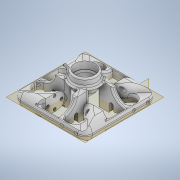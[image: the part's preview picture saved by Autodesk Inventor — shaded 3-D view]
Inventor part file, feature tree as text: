
AUTODESK INVENTOR PART (.ipt)
format: ipt  version: 2020 (Build 240168000, 168)  size: 1,643,520 bytes
history: native  units: mm
features: fillet x26, sketch x14, extrude x12, revolve x8, hole x4, plane x2, chamfer x1
ambient origin geometry x8: Origin, YZ Plane, XZ Plane, XY Plane, X Axis, Y Axis, Z Axis, Center Point
bodies: Solid1 (feature_tree)
feature tree (67):
  sketch  "Sketch1"  dims[d0=22.0mm d3=15.556349mm]
  revolve  "Revolution1"  [1 undecoded]
  revolve  "Revolution2"  [1 undecoded]
  revolve  "Revolution3"  [1 undecoded]
  revolve  "Revolution4"  [1 undecoded]
  plane  "Work Plane1"
  sketch  "Sketch2"  dims[d4=15.556349mm d5=40.0mm]
  extrude  "Extrusion2"  Depth=13.0mm
  chamfer  "Chamfer1"  Distance=40.0mm
  fillet  "Fillet2"  [1 undecoded]
  extrude  "Extrusion3"  TaperAngle=135.0deg  [1 undecoded]
  extrude  "Extrusion5"  Depth=5.0mm TaperAngle=360.0deg
  fillet  "Fillet3"  [1 undecoded]
  fillet  "Fillet4"  [1 undecoded]
  fillet  "Fillet5"  [1 undecoded]
  fillet  "Fillet6"  [1 undecoded]
  hole  "Hole2"  [1 undecoded]
  hole  "Hole3"  [1 undecoded]
  hole  "Hole4"  [1 undecoded]
  fillet  "Fillet7"  Radius=100.0mm
  hole  "Hole5"  [1 undecoded]
  plane  "Work Plane2"
  sketch  "Sketch13"  dims[d13=31.5mm]
  extrude  "Extrusion9"  Depth=5.0mm
  extrude  "Extrusion10"  Depth=10.0mm TaperAngle=0.0deg
  fillet  "Fillet8"  Radius=10.0mm
  fillet  "Fillet9"  Radius=2.0mm
  fillet  "Fillet10"  Radius=22.0mm
  revolve  "Revolution9"  [1 undecoded]
  revolve  "Revolution10"  [1 undecoded]
  revolve  "Revolution11"  [1 undecoded]
  revolve  "Revolution12"  [1 undecoded]
  extrude  "Extrusion11"  Depth=10.0mm
  fillet  "Fillet11"  Radius=16.0mm
  fillet  "Fillet12"  Radius=19.0mm
  fillet  "Fillet13"  Radius=19.0mm
  extrude  "Extrusion12"  Depth=5.0mm
  fillet  "Fillet14"  Radius=16.0mm
  fillet  "Fillet15"  Radius=19.0mm
  extrude  "Extrusion13"  Depth=5.0mm
  fillet  "Fillet17"  Radius=3.0mm
  fillet  "Fillet18"  Radius=19.0mm
  fillet  "Fillet19"  Radius=16.0mm
  fillet  "Fillet20"  Radius=40.0mm
  extrude  "Extrusion14"  Depth=5.0mm
  fillet  "Fillet21"  Radius=3.221825mm
  extrude  "Extrusion15"  Depth=5.0mm
  fillet  "Fillet22"  Radius=28.0mm
  extrude  "Extrusion16"  Depth=5.0mm
  fillet  "Fillet23"  Radius=6.0mm
  fillet  "Fillet24"  Radius=6.0mm
  extrude  "Extrusion17"  Depth=5.0mm
  fillet  "Fillet25"  Radius=21.0mm
  fillet  "Fillet26"  Radius=10.0mm
  fillet  "Fillet30"  Radius=20.0mm
  fillet  "Fillet31"  Radius=6.0mm
  sketch  "Sketch3"  dims[d6=3.221825mm d7=3.222mm]
  sketch  "Sketch4"  dims[d8=18.5mm d9=28.0mm]
  sketch  "Sketch6"  dims[d10=4.0mm d11=13.0mm]
  sketch  "Sketch7"  dims[d12=5.0mm]
  sketch  "Sketch14"  dims[d14=2.778175mm]
  sketch  "Sketch16"  dims[d15=2.778mm]
  sketch  "Sketch17"  dims[d16=14.0mm]
  sketch  "Sketch18"  dims[d17=19.0mm]
  sketch  "Sketch19"  dims[d18=3.0mm]
  sketch  "Sketch20"  dims[d19=25.0mm]
  sketch  "Sketch21"  dims[d20=135.0deg d21=40.0mm d22=135.0deg d23=135.0deg d24=40.0mm d26=360.0deg d28=90.0deg d29=90.0deg d30=90.0deg d31=90.0deg d38=19.0mm d39=16.0mm d50=100.0mm d51=100.0mm d52=96.0mm d53=96.0mm d54=10.0mm d55=0.0mm d56=10.0mm d57=2.0mm d58=45.0deg d59=2.0mm d60=22.0mm d61=0.0mm d64=22.0mm d65=0.0mm d66=10.0mm d67=10.0mm d68=10.0mm d69=10.0mm d70=16.0mm d71=19.0mm d72=4.134mm d73=10.0mm d74=4.0mm d75=2.0mm d76=90.0deg d77=8.0mm d78=20.594885mm d79=19.0mm d80=16.0mm d81=16.0mm d82=4.134mm d83=10.0mm d84=4.0mm d85=2.0mm d86=90.0deg d87=8.0mm d88=20.594885mm d91=19.0mm d92=16.0mm d93=4.134mm d94=10.0mm d95=4.0mm d96=2.0mm d97=90.0deg d98=8.0mm d99=20.594885mm d100=3.0mm d101=19.0mm d102=16.0mm d103=4.134mm d104=10.0mm d105=4.0mm d106=2.0mm d107=90.0deg d108=8.0mm d109=20.594885mm d110=40.0mm d111=15.556349mm d112=3.221825mm d113=11.556349mm d114=28.0mm d115=13.0mm d127=6.0mm d130=6.0mm d131=4.0mm d132=21.0mm d133=0.0mm d134=10.0mm d135=0.0mm d136=20.0mm d137=6.0mm d138=22.0mm d139=40.0mm d141=360.0deg d143=20.0mm d144=90.0deg d145=90.0deg d146=90.0deg d147=90.0deg d148=23.0mm d149=40.0mm d150=3.0mm d151=0.0mm d152=20.0mm d153=2.0mm d154=2.0mm d155=2.0mm d156=0.0mm d157=28.0mm d158=32.0mm d159=10.0mm d160=0.0mm d161=2.0mm d162=2.0mm d163=23.0mm d164=28.0mm d165=8.0mm d166=0.0mm d168=2.0mm d169=2.0mm d170=11.0mm d171=0.0mm d172=2.0mm d173=2.0mm d174=10.0mm d175=0.0mm d176=2.0mm d177=10.0mm d178=0.0mm d179=2.0mm d180=5.0mm d181=10.0mm d182=0.0mm d183=2.0mm d184=2.0mm d185=5.0mm d186=10.0mm d187=0.0mm d188=2.0mm d189=2.0mm d190=19.06362mm d191=25.0mm d192=25.0mm d193=25.0mm d194=25.0mm d198=5.0mm d199=5.0mm d195=0.5mm d196=0.872665mm d197=0.5mm]
note: 18 required parameter values undecoded (feature->parameter linkage not recoverable at this tier; creation-order binding heuristic only, values carry confidence <= 0.55)